# Revit family: DCS-Revit18-RF15IL3-Outdoor-Ice-Maker-0-9000xxxxA
name_source: partatom
category: Specialty Equipment
revit_build: Autodesk Revit 2018 (Build: 20170223_1515(x64)
units: mm (PartAtom-declared; Revit-internal decimal feet)

## family parameters
Always vertical = Yes
Cut with Voids When Loaded = Yes
OmniClass Number = 23.40.40.00
OmniClass Title = Food Service Equipment and Furnishings
Part Type = Normal
Room Calculation Point = No
Round Connector Dimension = Use Diameter
Shared = No
Work Plane-Based = No

## types (1)
- RF15IL3
    Cavity - Depth = 613 mm  [stored 2.01115 ft]
    Cavity - Height (863mm to 889mm) = 863 mm  [stored 2.83136 ft]
    Cavity - Width = 381 mm  [stored 1.25 ft]
    Chassis - Depth = 546 mm  [stored 1.79134 ft]
    Chassis - Height = 854 mm  [stored 2.80184 ft]
    Chassis - Width = 378 mm  [stored 1.24016 ft]
    Connector Description - Electrical = 115 V, 60 Hz, 15 A dedicated circuit
    Connector Description - Sanitary = Sanitary Trap required close by
    Connector Description - Water = 1/4" copper tubing, 20 - 120 psi MAX
    Description = Outdoor Ice Maker
    Manufacturer = Fisher & Paykel Appliances
    Material - Body = DCS - Grey
    Material - Door Front = DCS - Stainless Steel
    Material - Handle = DCS - Aluminium
    Model = RF15IL3
    Product - Depth = 643 mm  [stored 2.10958 ft]
    Product - Height (857mm to 883mm) = 857 mm  [stored 2.81168 ft]
    Product - Width = 378 mm  [stored 1.24016 ft]
    URL = www.dcsappliances.com
    Visibility - Clearance Required = Yes

note: [stored X ft] marks values corroborated as IEEE doubles in the binary element streams (Revit-internal decimal feet)

## geometry (parser evidence)
native form markers: Sweep x4
no freeform markers — native parametric forms only
